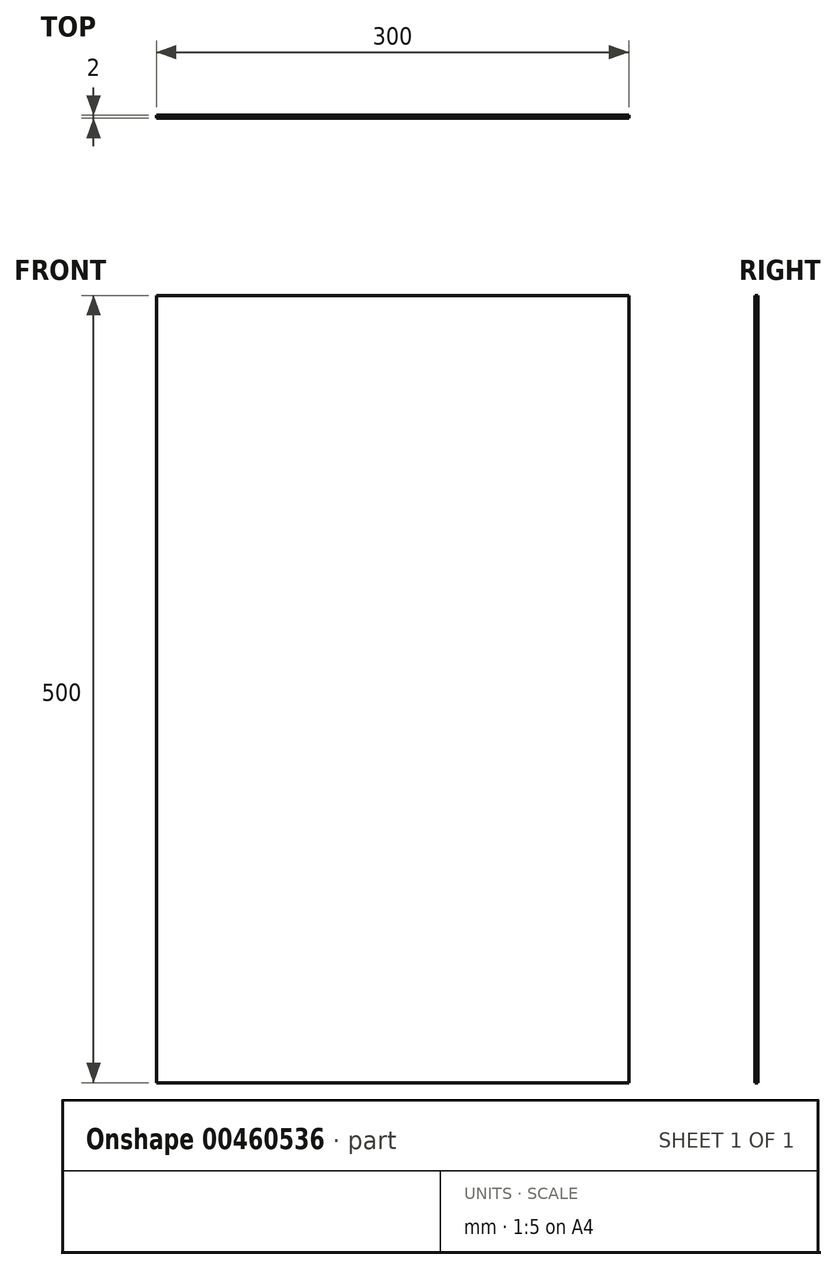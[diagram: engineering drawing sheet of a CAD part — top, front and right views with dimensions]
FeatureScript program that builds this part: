
annotation { "Feature Type Name" : "Feature", "Feature Type Description" : "" }
export const myFeature = defineFeature(function(context is Context, id is Id, definition is map)
    precondition{}
    {
        {
            var Q0;
            Q0=qCreatedBy(makeId("Front.planeOp"),FACE);
            var sketch = newSketch(context, id + "F0", { "sketchPlane" : qUnion([Q0])});
            skLineSegment(sketch, "E0.bottom", {"start": v(-162.2, 346.92) * mm, "end": v(137.8, 346.92) * mm});
            skLineSegment(sketch, "E0.top", {"start": v(-162.2, -153.08) * mm, "end": v(137.8, -153.08) * mm});
            skLineSegment(sketch, "E0.left", {"start": v(-162.2, 346.92) * mm, "end": v(-162.2, -153.08) * mm});
            skLineSegment(sketch, "E0.right", {"start": v(137.8, 346.92) * mm, "end": v(137.8, -153.08) * mm});
            skSolve(sketch);
        }
        {
            var Q0;
            Q0 = qSketchRegion(id + "F0", true);
            extrude(context, id + "F1", {"entities" : qUnion([Q0]), "depth" : 2 * mm});
        }
    });
